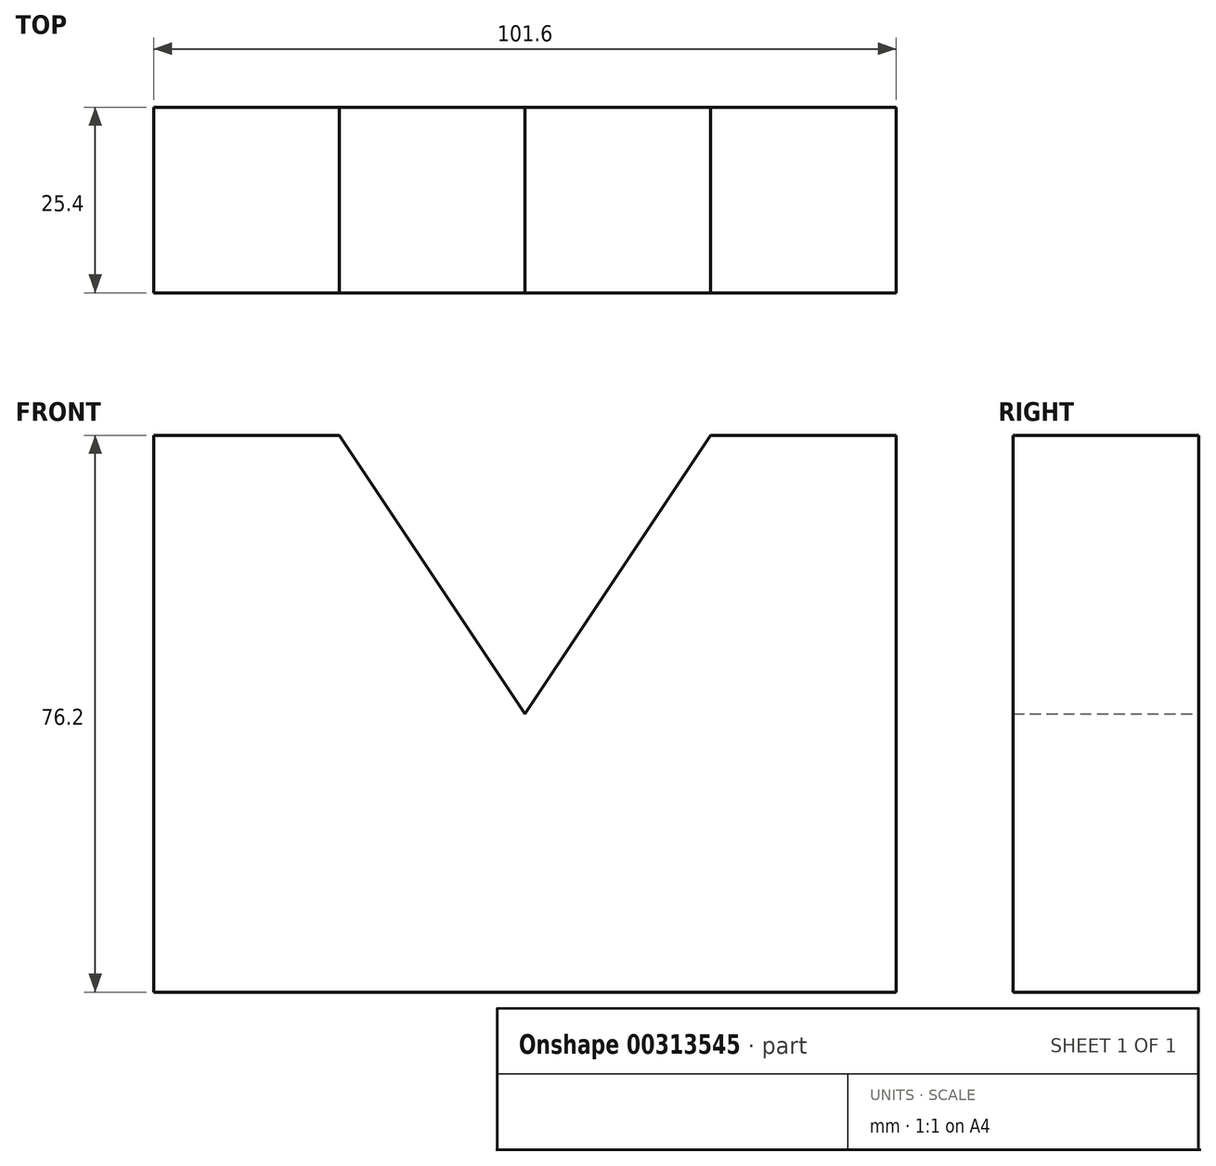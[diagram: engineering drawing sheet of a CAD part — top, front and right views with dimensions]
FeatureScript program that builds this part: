
annotation { "Feature Type Name" : "Feature", "Feature Type Description" : "" }
export const myFeature = defineFeature(function(context is Context, id is Id, definition is map)
    precondition{}
    {
        {
            var Q0;
            Q0=qCreatedBy(makeId("Front.planeOp"),FACE);
            var sketch = newSketch(context, id + "F0", { "sketchPlane" : qUnion([Q0])});
            skLineSegment(sketch, "E0", {"start": v(-53.74, -42.28) * mm, "end": v(47.86, -42.28) * mm});
            skLineSegment(sketch, "E1", {"start": v(47.86, -42.28) * mm, "end": v(47.86, 33.92) * mm});
            skLineSegment(sketch, "E2", {"start": v(-53.74, -42.28) * mm, "end": v(-53.74, 33.92) * mm});
            skLineSegment(sketch, "E3", {"start": v(-53.74, 33.92) * mm, "end": v(-28.34, 33.92) * mm});
            skLineSegment(sketch, "E4", {"start": v(47.86, 33.92) * mm, "end": v(22.46, 33.92) * mm});
            skPoint(sketch, "E5", {"position": v(-2.94, -4.18) * mm});
            skLineSegment(sketch, "E6", {"start": v(22.46, 33.92) * mm, "end": v(-2.94, -4.18) * mm});
            skLineSegment(sketch, "E7", {"start": v(-28.34, 33.92) * mm, "end": v(-2.94, -4.18) * mm});
            skSolve(sketch);
        }
        {
            var Q0;
            Q0 = qSketchRegion(id + "F0", true);
            extrude(context, id + "F1", {"entities" : qUnion([Q0]), "depth" : 25.4 * mm});
        }
    });
